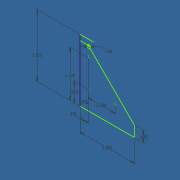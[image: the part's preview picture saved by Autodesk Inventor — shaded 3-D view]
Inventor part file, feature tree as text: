
AUTODESK INVENTOR PART (.ipt)
format: ipt  version: unknown  size: 158,720 bytes
history: native  units: in
note: dims shown in document units (in); Inventor stores cm internally (conversion verified against a paired STEP export)
features: sketch x1
ambient origin geometry x8: Origin, YZ Plane, XZ Plane, XY Plane, X Axis, Y Axis, Z Axis, Center Point
feature tree (1):
  sketch  "Sketch1"  dims[d0=2.875in d2=0.5in d3=2.5in d6=0.1562in d7=2.125in d8=0.375in d9=0.375in d10=1.25in d11=0.875in]
